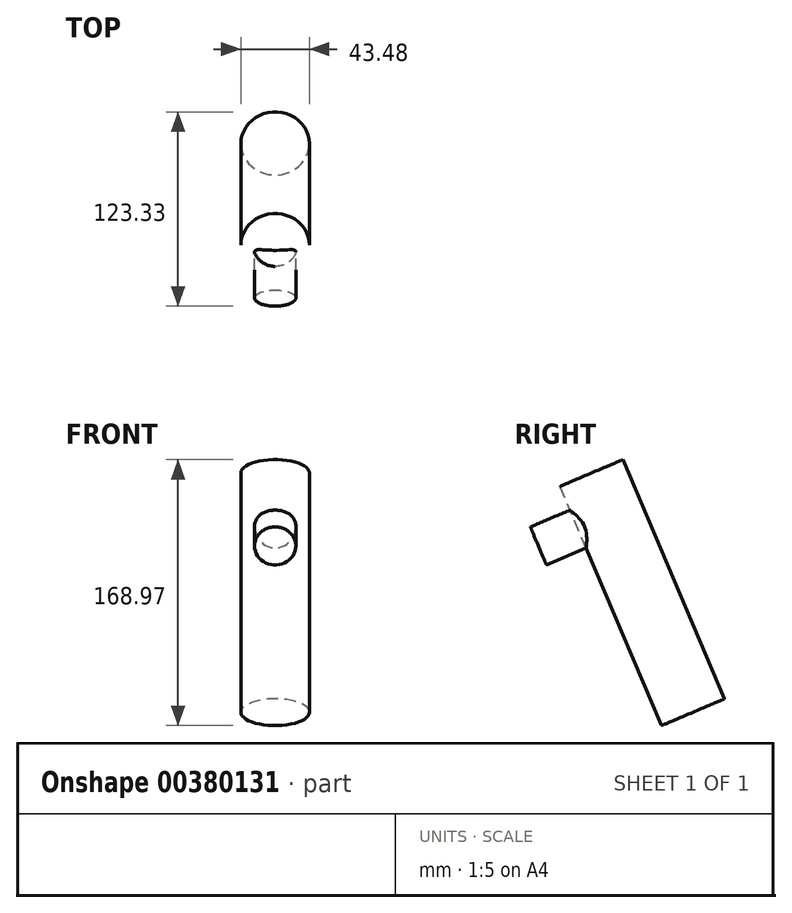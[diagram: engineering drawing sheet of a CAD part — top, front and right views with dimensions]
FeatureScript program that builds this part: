
annotation { "Feature Type Name" : "Feature", "Feature Type Description" : "" }
export const myFeature = defineFeature(function(context is Context, id is Id, definition is map)
    precondition{}
    {
        {
            var Q0;
            Q0=qCreatedBy(makeId("Top.planeOp"),FACE);
            var sketch = newSketch(context, id + "F0", { "sketchPlane" : qUnion([Q0])});
            skCircle(sketch, "E0", {"center": v(0, 49.1) * mm, "radius": 21.74 * mm});
            skSolve(sketch);
        }
        {
            var Q0;
            Q0=sQuery(id+"F0.wireOp",EDGE,"E0");
            extrude(context, id + "F1", {"bodyType" : ToolBodyType.SURFACE, "surfaceEntities" : qUnion([Q0]), "depth" : 165.1 * mm});
        }
        {
            var Q0;
            Q0=qCreatedBy(makeId("Right.planeOp"),FACE);
            var sketch = newSketch(context, id + "F2", { "sketchPlane" : qUnion([Q0])});
            skFitSpline(sketch, "E1", {"points": [v(27.49, 133) * mm, v(-77.33, 141.57) * mm, v(-194.16, 130.65) * mm, v(-325.77, 112.05) * mm, v(-531.15, 105.2) * mm, v(-759.6, 142.45) * mm, v(-977.74, 204.57) * mm], "startDerivative": vector(-777.89, 97.84) * mm, "endDerivative": vector(-1108.35, 338.39) * mm});
            skSolve(sketch);
        }
        {
            var Q0;
            Q0=qCreatedBy(makeId("Front.planeOp"),FACE);
            var sketch = newSketch(context, id + "F3", { "sketchPlane" : qUnion([Q0])});
            skCircle(sketch, "E2", {"center": v(0, 135.6) * mm, "radius": 13.1 * mm});
            skSolve(sketch);
        }
        {
            var Q0;
            Q0=sQuery(id+"F3.wireOp",EDGE,"E2");
            extrude(context, id + "F4", {"bodyType" : ToolBodyType.SURFACE, "surfaceEntities" : qUnion([Q0]), "endBound" : BoundingType.UP_TO_NEXT, "oppositeDirection" : true, "depth" : 151.88 * mm});
        }
        {
            var Q0;
            Q0=qCreatedBy(makeId("Right.planeOp"),FACE);
            var sketch = newSketch(context, id + "F5", { "sketchPlane" : qUnion([Q0])});
            skCircle(sketch, "E3", {"center": v(45.96, -24.32) * mm, "radius": 19.42 * mm});
            skSolve(sketch);
        }
        {
            var Q0;
            Q0=sQuery(id+"F5.wireOp",EDGE,"E3");
            extrude(context, id + "F6", {"bodyType" : ToolBodyType.SURFACE, "surfaceEntities" : qUnion([Q0]), "depth" : 108.84 * mm});
        }
        {
            var Q0;
            Q0=makeQuery(id+"F1.opExtrude","SWEPT_BODY",BODY,{"disambiguationData":[OSD([sQuery(id+"F0.wireOp",EDGE,"E0")])]});
            var Q1;
            Q1=makeQuery(id+"F4.opExtrude","SWEPT_BODY",BODY,{"disambiguationData":[OSD([sQuery(id+"F3.wireOp",EDGE,"E2")])]});
            var Q2;
            Q2=makeQuery(id+"F409E8q4Hb6m4Ni_2.opSweep","SWEPT_BODY",BODY,{"disambiguationData":[OSD([sQuery(id+"F2.wireOp",EDGE,"E1"),sQuery(id+"F3.wireOp",EDGE,"E2")])]});
            var Q3;
            Q3=makeQuery(id+"F6.opExtrude","CAP_EDGE",EDGE,{"disambiguationData":[OSD([sQuery(id+"F5.wireOp",EDGE,"E3")])],"isStart":true});
            transform(context, id + "F7", {"entities" : qUnion([Q0, Q1, Q2]), "transformType" : TransformType.ROTATION, "transformAxis" : qUnion([Q3]), "angle" : 23 * degree, "makeCopy" : false});
        }
        {
            var Q0;
            Q0=makeQuery(id+"F6.opExtrude","SWEPT_BODY",BODY,{"disambiguationData":[OSD([sQuery(id+"F5.wireOp",EDGE,"E3")])]});
            deleteBodies(context, id + "F8", {"entities" : qUnion([Q0])});
        }
    });
